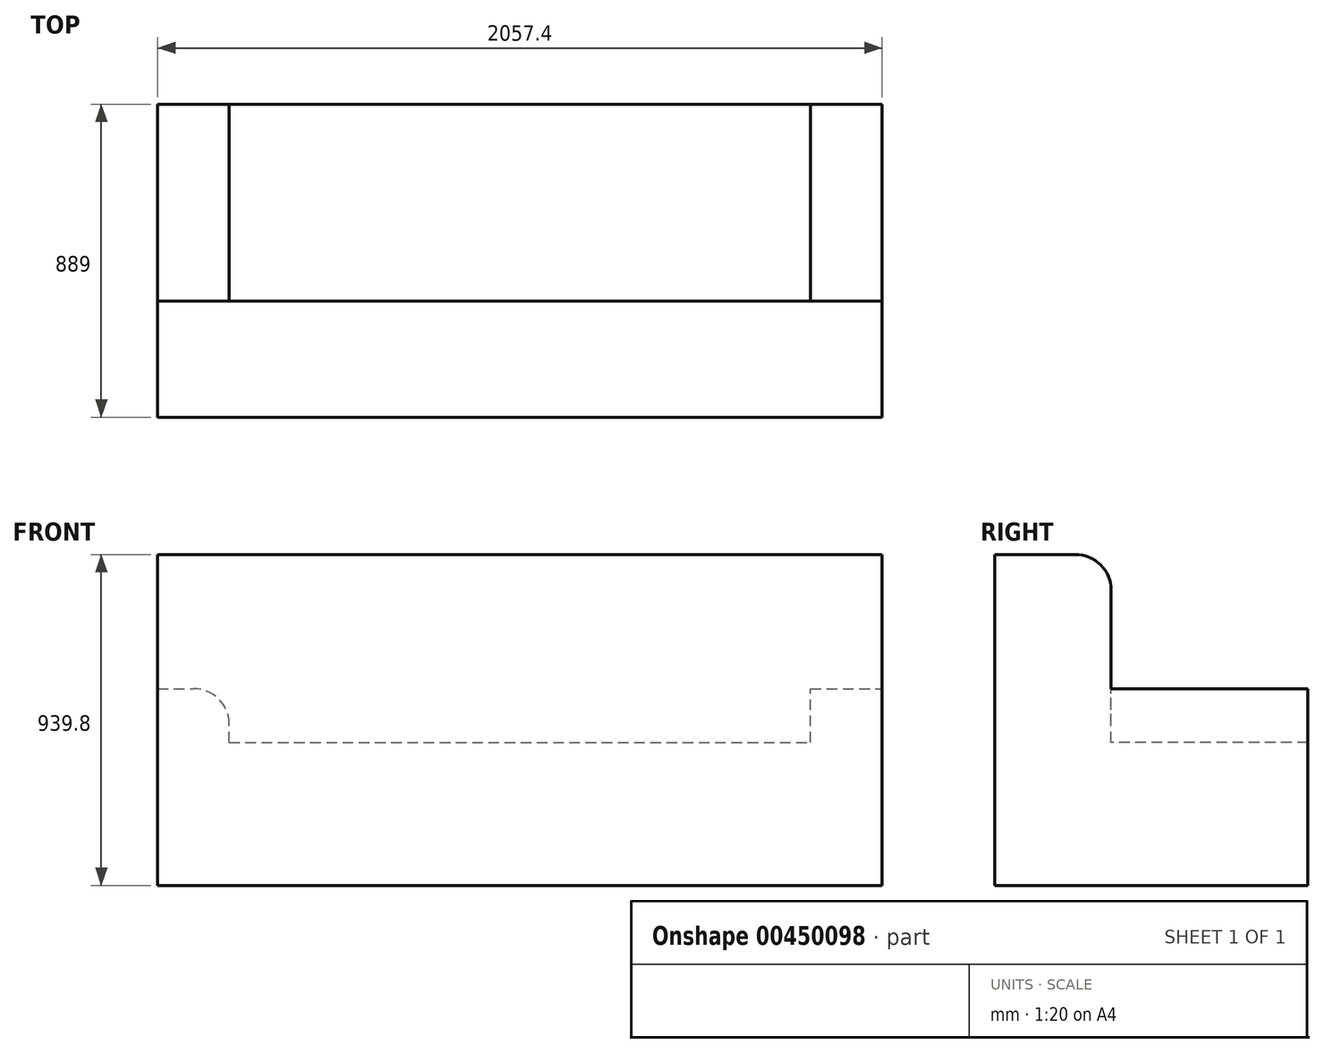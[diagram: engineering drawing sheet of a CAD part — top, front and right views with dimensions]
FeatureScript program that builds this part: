
annotation { "Feature Type Name" : "Feature", "Feature Type Description" : "" }
export const myFeature = defineFeature(function(context is Context, id is Id, definition is map)
    precondition{}
    {
        {
            var Q0;
            Q0=qCreatedBy(makeId("Right.planeOp"),FACE);
            var sketch = newSketch(context, id + "F0", { "sketchPlane" : qUnion([Q0])});
            skLineSegment(sketch, "E0", {"start": v(0, 0) * mm, "end": v(0, 939.8) * mm});
            skLineSegment(sketch, "E1", {"start": v(0, 939.8) * mm, "end": v(330.2, 939.8) * mm});
            skLineSegment(sketch, "E2", {"start": v(330.2, 939.8) * mm, "end": v(330.2, 558.8) * mm});
            skLineSegment(sketch, "E3", {"start": v(330.2, 558.8) * mm, "end": v(889, 558.8) * mm});
            skLineSegment(sketch, "E4", {"start": v(889, 558.8) * mm, "end": v(889, 0) * mm});
            skLineSegment(sketch, "E5", {"start": v(889, 0) * mm, "end": v(0, 0) * mm});
            skSolve(sketch);
        }
        {
            var Q0;
            Q0=makeQuery(id+"F0.imprint","IMPRINT",FACE,{"disambiguationData":[TD([[makeQuery(id+"F0.imprint","IMPRINT",EDGE,{"derivedFrom":sQuery(id+"F0.wireOp",EDGE,"E0")}),-1.0]])]});
            extrude(context, id + "F1", {"entities" : qUnion([Q0]), "oppositeDirection" : true, "depth" : 2057.4 * mm});
        }
        {
            var Q0;
            Q0=makeQuery(id+"F1.opExtrude","SWEPT_FACE",FACE,{"disambiguationData":[OSD([sQuery(id+"F0.wireOp",EDGE,"E3")])]});
            var sketch = newSketch(context, id + "F2", { "sketchPlane" : qUnion([Q0])});
            skLineSegment(sketch, "E6.bottom", {"start": v(-1854.2, 889) * mm, "end": v(-203.2, 889) * mm});
            skLineSegment(sketch, "E6.top", {"start": v(-1854.2, 330.2) * mm, "end": v(-203.2, 330.2) * mm});
            skLineSegment(sketch, "E6.left", {"start": v(-1854.2, 889) * mm, "end": v(-1854.2, 330.2) * mm});
            skLineSegment(sketch, "E6.right", {"start": v(-203.2, 889) * mm, "end": v(-203.2, 330.2) * mm});
            skLineSegment(sketch, "E7", {"start": v(-1854.2, 609.6) * mm, "end": v(-2057.4, 609.6) * mm, "construction": true});
            skLineSegment(sketch, "E8", {"start": v(-203.2, 609.6) * mm, "end": v(0, 609.6) * mm, "construction": true});
            skSolve(sketch);
        }
        {
            var Q0;
            Q0=makeQuery(id+"F2.imprint","IMPRINT",FACE,{"disambiguationData":[TD([[makeQuery(id+"F2.imprint","IMPRINT",EDGE,{"derivedFrom":sQuery(id+"F2.wireOp",EDGE,"E6.bottom")}),-1.0]])]});
            extrude(context, id + "F3", {"entities" : qUnion([Q0]), "operationType" : NewBodyOperationType.REMOVE, "oppositeDirection" : true, "depth" : 152.4 * mm});
        }
        {
            var Q0;
            Q0=makeQuery(id+"F3.boolean.opBoolean","COPY",EDGE,{"derivedFrom":makeQuery(id+"F3.opExtrude","CAP_EDGE",EDGE,{"disambiguationData":[OSD([sQuery(id+"F2.wireOp",EDGE,"E6.bottom")])],"isStart":false})});
            var Q1;
            Q1=makeQuery(id+"F1.opExtrude","SWEPT_EDGE",EDGE,{"disambiguationData":[OSD([sQuery(id+"F0.wireOp",EDGE,"E1"),sQuery(id+"F0.wireOp",EDGE,"E2")])]});
            var Q2;
            Q2=makeQuery(id+"F3.boolean.opBoolean","COPY",EDGE,{"derivedFrom":makeQuery(id+"F3.opExtrude","CAP_EDGE",EDGE,{"disambiguationData":[OSD([sQuery(id+"F2.wireOp",EDGE,"E6.right")])],"isStart":true})});
            var Q3;
            Q3=makeQuery(id+"F3.boolean.opBoolean","COPY",EDGE,{"derivedFrom":makeQuery(id+"F3.opExtrude","CAP_EDGE",EDGE,{"disambiguationData":[OSD([sQuery(id+"F2.wireOp",EDGE,"E6.left")])],"isStart":true})});
            fillet(context, id + "F4", {"entities" : qUnion([Q0, Q1, Q2, Q3]), "radius" : 101.6 * mm, "tangentPropagation" : true, "allowEdgeOverflow" : false});
        }
    });
